# Revit family: Haworth_Enclose_Accessories_WallTransitionPost
name_source: partatom
category: Furniture Systems
revit_build: Autodesk Revit 2018 (Build: 20170223_1515(x64)
units: mm (PartAtom-declared; Revit-internal decimal feet)

## family parameters
Always vertical = Yes
Cut with Voids When Loaded = No
OmniClass Number = 23.25.40.14
OmniClass Title = Demountable Partitions
Part Type = Normal
Room Calculation Point = No
Round Connector Dimension = Use Diameter
Shared = No
Work Plane-Based = No

## types (2) — shared parameters
Actual Height = 108 "
Assembly Code = C1010200
Depth = 4 "
Description = Wall Transition Post
Frame Finish = Haworth _ Metal _ Brushed Aluminum
Height = 108 "
Manufacturer = Haworth
Material Options = http://surfaces.haworth.com
Max. Height = 144 "
Min. Height = 84 "
Min/Max Height = 84-144 in.
Model = Haworth - Enclose Accessories
Revision Number = 3
Sustainability Info = http://www.haworth.com
URL = www.haworth.com
URL - Product = http://www.haworth.com
Warranty = http://www.haworth.com
Width = 2.69 "

## type names (no varying parameters)
- 3 Way - 90
- 2 Way - 90

## geometry (parser evidence)
native form markers: Sweep x3
no freeform markers — native parametric forms only
